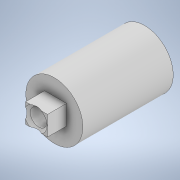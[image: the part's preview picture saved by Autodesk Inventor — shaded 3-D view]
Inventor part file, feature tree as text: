
AUTODESK INVENTOR PART (.ipt)
format: ipt  version: 2020 (Build 240168000, 168)  size: 147,456 bytes
history: native  units: in
note: dims shown in document units (in); Inventor stores cm internally (conversion verified against a paired STEP export)
features: sketch x6, extrude x4, chamfer x2, hole x1
ambient origin geometry x8: Origin, YZ Plane, XZ Plane, XY Plane, X Axis, Y Axis, Z Axis, Center Point
bodies: Solid1 (feature_tree)
feature tree (13):
  sketch  "Sketch1"  dims[d0=2.4in d1=4.6in d2=0.0in]
  extrude  "Extrusion1"  Depth=4.6in TaperAngle=0.0deg
  extrude  "Extrusion2"  Depth=3.5in TaperAngle=0.0deg
  hole  "Hole1"  [1 undecoded]
  extrude  "Extrusion3"  Depth=3.5in
  chamfer  "Chamfer1"  [1 undecoded]
  chamfer  "Chamfer2"  [1 undecoded]
  extrude  "Extrusion4"  [1 undecoded]
  sketch  "Sketch2"  dims[d3=0.8in d4=0.0in]
  sketch  "Sketch3"  dims[d5=0.7087in d6=0.75in d7=0.375in d8=0.25in d9=0.5635in d10=1.0in d11=0.8108in d12=3.5in d13=0.0in]
  sketch  "Sketch4"  dims[d14=0.125in d15=0.125in d16=45.0deg d17=0.1969in d18=0.125in d19=45.0deg]
  sketch  "Sketch5"  dims[d20=3.5in d21=0.0in d22=0.5in]
  sketch  "Sketch6"  dims[d23=0.0344in]
note: 4 required parameter values undecoded (feature->parameter linkage not recoverable at this tier; creation-order binding heuristic only, values carry confidence <= 0.55)
